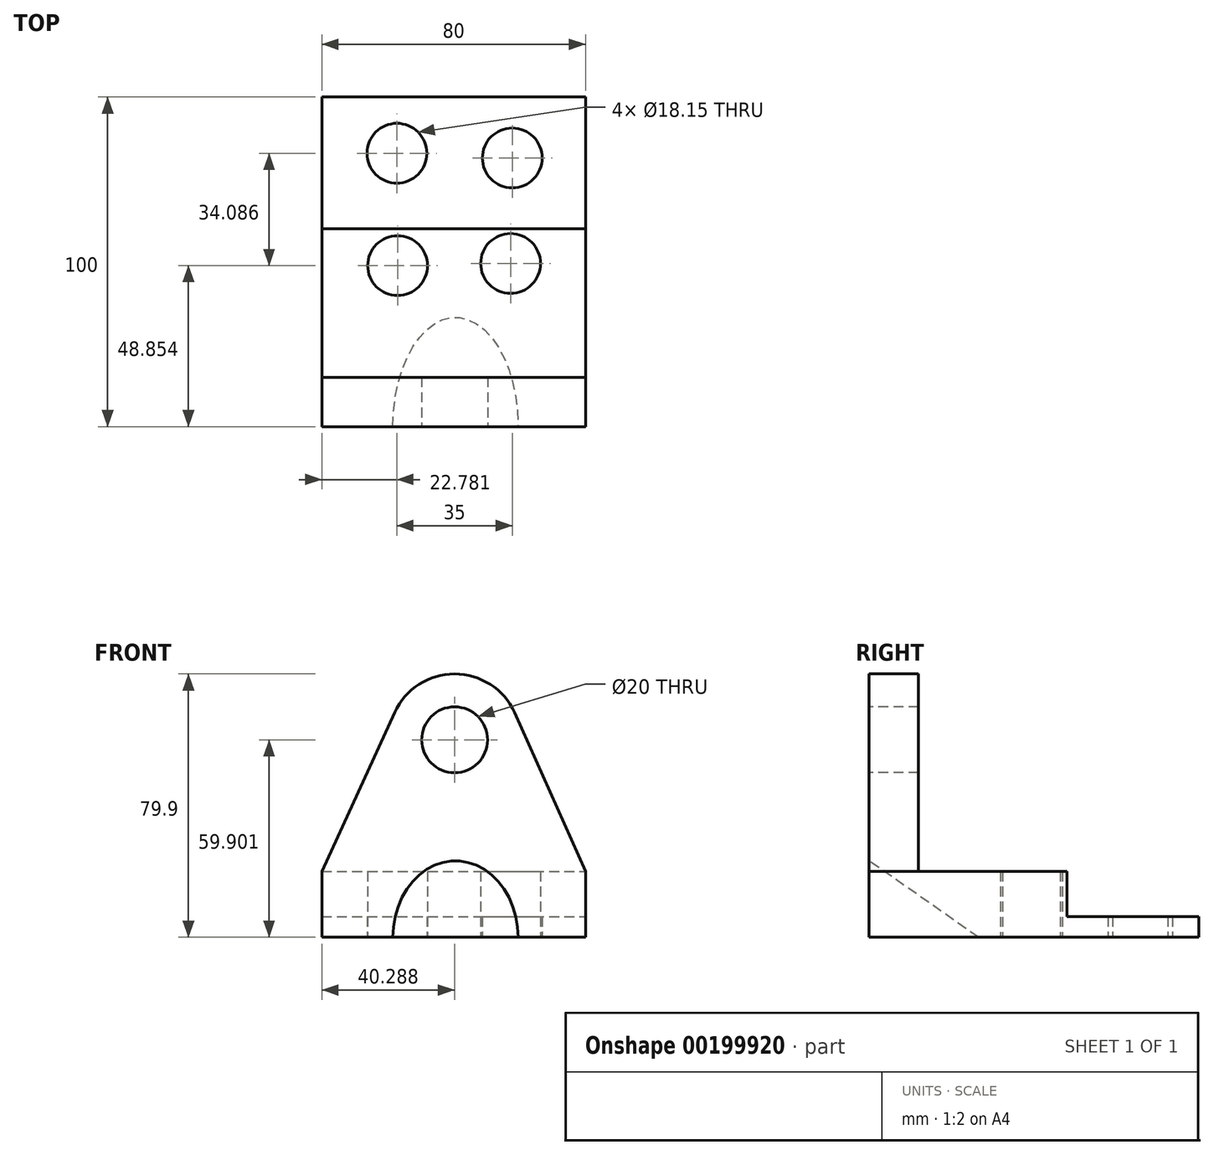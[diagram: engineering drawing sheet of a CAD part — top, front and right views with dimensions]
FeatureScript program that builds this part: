
annotation { "Feature Type Name" : "Feature", "Feature Type Description" : "" }
export const myFeature = defineFeature(function(context is Context, id is Id, definition is map)
    precondition{}
    {
        {
            var Q0;
            Q0=qCreatedBy(makeId("Front.planeOp"),FACE);
            var sketch = newSketch(context, id + "F0", { "sketchPlane" : qUnion([Q0])});
            skLineSegment(sketch, "E0", {"start": v(-33.48, 0) * mm, "end": v(46.52, 0) * mm});
            skLineSegment(sketch, "E1", {"start": v(-33.48, 0) * mm, "end": v(-33.48, 20) * mm});
            skLineSegment(sketch, "E2", {"start": v(-33.48, 20) * mm, "end": v(46.52, 20) * mm});
            skLineSegment(sketch, "E3", {"start": v(46.52, 20) * mm, "end": v(46.52, 0) * mm});
            skCircle(sketch, "E4", {"center": v(6.8, 59.9) * mm, "radius": 20 * mm});
            skLineSegment(sketch, "E5", {"start": v(-33.48, 20) * mm, "end": v(-11.37, 68.23) * mm});
            skLineSegment(sketch, "E6", {"start": v(-11.37, 68.23) * mm, "end": v(24.99, 68.23) * mm});
            skLineSegment(sketch, "E7", {"start": v(24.99, 68.23) * mm, "end": v(46.52, 20) * mm});
            skCircle(sketch, "E8", {"center": v(6.8, 59.9) * mm, "radius": 10 * mm});
            skLineSegment(sketch, "E9", {"start": v(-33.48, 6.28) * mm, "end": v(46.52, 6.28) * mm});
            skSolve(sketch);
        }
        {
            var Q0;
            {var subQ0=sQuery(id+"F0.wireOp",EDGE,"E0");Q0=makeQuery(id+"F0.imprint","IMPRINT",FACE,{"disambiguationData":[TD([[makeQuery(id+"F0.imprint","IMPRINT",EDGE,{"derivedFrom":subQ0}),1.0]])]});}
            extrude(context, id + "F1", {"entities" : qUnion([Q0]), "oppositeDirection" : true, "depth" : 100 * mm});
        }
        {
            var Q0;
            {var subQ0=sQuery(id+"F0.wireOp",EDGE,"E2");Q0=makeQuery(id+"F0.imprint","IMPRINT",FACE,{"disambiguationData":[TD([[makeQuery(id+"F0.imprint","IMPRINT",EDGE,{"derivedFrom":subQ0}),-1.0]])]});}
            extrude(context, id + "F2", {"entities" : qUnion([Q0]), "operationType" : NewBodyOperationType.ADD, "oppositeDirection" : true, "depth" : 60 * mm});
        }
        {
            var Q0;
            {var subQ0=sQuery(id+"F0.wireOp",EDGE,"E2");Q0=makeQuery(id+"F0.imprint","IMPRINT",FACE,{"disambiguationData":[TD([[makeQuery(id+"F0.imprint","IMPRINT",EDGE,{"derivedFrom":subQ0}),1.0]])]});}
            var Q1;
            {var subQ1=sQuery(id+"F0.wireOp",EDGE,"E6");var subQ5=sQuery(id+"F0.wireOp",EDGE,"E8");var subQ7=makeQuery(id+"F0.imprint","INTERSECT",VERTEX,{"disambiguationData":[OD(0.0)],"derivedFrom":[subQ1,subQ5]});Q1=makeQuery(id+"F0.imprint","IMPRINT",FACE,{"disambiguationData":[TD([[makeQuery(id+"F0.imprint","IMPRINT",EDGE,{"disambiguationData":[TD([[subQ7,-1.0]])],"derivedFrom":subQ5}),-1.0]])]});}
            var Q2;
            {var subQ0=sQuery(id+"F0.wireOp",EDGE,"E6");var subQ4=sQuery(id+"F0.wireOp",EDGE,"E8");var subQ5=makeQuery(id+"F0.imprint","INTERSECT",VERTEX,{"disambiguationData":[OD(0.0)],"derivedFrom":[subQ0,subQ4]});Q2=makeQuery(id+"F0.imprint","IMPRINT",FACE,{"disambiguationData":[TD([[makeQuery(id+"F0.imprint","IMPRINT",EDGE,{"disambiguationData":[TD([[subQ5,1.0]])],"derivedFrom":subQ4}),-1.0]])]});}
            extrude(context, id + "F3", {"entities" : qUnion([Q0, Q1, Q2]), "operationType" : NewBodyOperationType.ADD, "oppositeDirection" : true, "depth" : 15 * mm});
        }
        {
            var Q0;
            Q0=qCreatedBy(makeId("Top.planeOp"),FACE);
            var sketch = newSketch(context, id + "F4", { "sketchPlane" : qUnion([Q0])});
            skCircle(sketch, "E10", {"center": v(24.3, 81.5) * mm, "radius": 9.08 * mm});
            skCircle(sketch, "E11", {"center": v(23.8, 49.5) * mm, "radius": 9.08 * mm});
            skCircle(sketch, "E12", {"center": v(-10.7, 82.94) * mm, "radius": 9.08 * mm});
            skCircle(sketch, "E13", {"center": v(-10.5, 48.85) * mm, "radius": 9.08 * mm});
            skSolve(sketch);
        }
        {
            var Q0;
            Q0=makeQuery(id+"F4.imprint","IMPRINT",FACE,{"disambiguationData":[TD([[makeQuery(id+"F4.imprint","IMPRINT",EDGE,{"derivedFrom":sQuery(id+"F4.wireOp",EDGE,"E11")}),1.0]])]});
            var Q1;
            Q1=makeQuery(id+"F4.imprint","IMPRINT",FACE,{"disambiguationData":[TD([[makeQuery(id+"F4.imprint","IMPRINT",EDGE,{"derivedFrom":sQuery(id+"F4.wireOp",EDGE,"E10")}),1.0]])]});
            var Q2;
            Q2=makeQuery(id+"F4.imprint","IMPRINT",FACE,{"disambiguationData":[TD([[makeQuery(id+"F4.imprint","IMPRINT",EDGE,{"derivedFrom":sQuery(id+"F4.wireOp",EDGE,"E12")}),1.0]])]});
            var Q3;
            Q3=makeQuery(id+"F4.imprint","IMPRINT",FACE,{"disambiguationData":[TD([[makeQuery(id+"F4.imprint","IMPRINT",EDGE,{"derivedFrom":sQuery(id+"F4.wireOp",EDGE,"E13")}),1.0]])]});
            extrude(context, id + "F5", {"entities" : qUnion([Q0, Q1, Q2, Q3]), "operationType" : NewBodyOperationType.REMOVE, "depth" : 25 * mm});
        }
        {
            var Q0;
            Q0=sQuery(id+"F0.wireOp",EDGE,"E0");
            cPlane(context, id + "F6", {"entities" : qUnion([Q0]), "cplaneType" : CPlaneType.LINE_ANGLE, "offset" : 25 * mm, "angle" : 145 * degree, "width" : 150 * mm, "height" : 150 * mm});
        }
        {
            var Q0;
            Q0=qCreatedBy(id+"F6.planeOp",FACE);
            var sketch = newSketch(context, id + "F7", { "sketchPlane" : qUnion([Q0])});
            skCircle(sketch, "E14", {"center": v(7.07, 0) * mm, "radius": 19 * mm});
            skSolve(sketch);
        }
        {
            var Q0;
            Q0 = qSketchRegion(id + "F7", true);
            extrude(context, id + "F8", {"entities" : qUnion([Q0]), "operationType" : NewBodyOperationType.REMOVE, "endBound" : BoundingType.SYMMETRIC, "oppositeDirection" : true, "depth" : 100 * mm});
        }
    });
